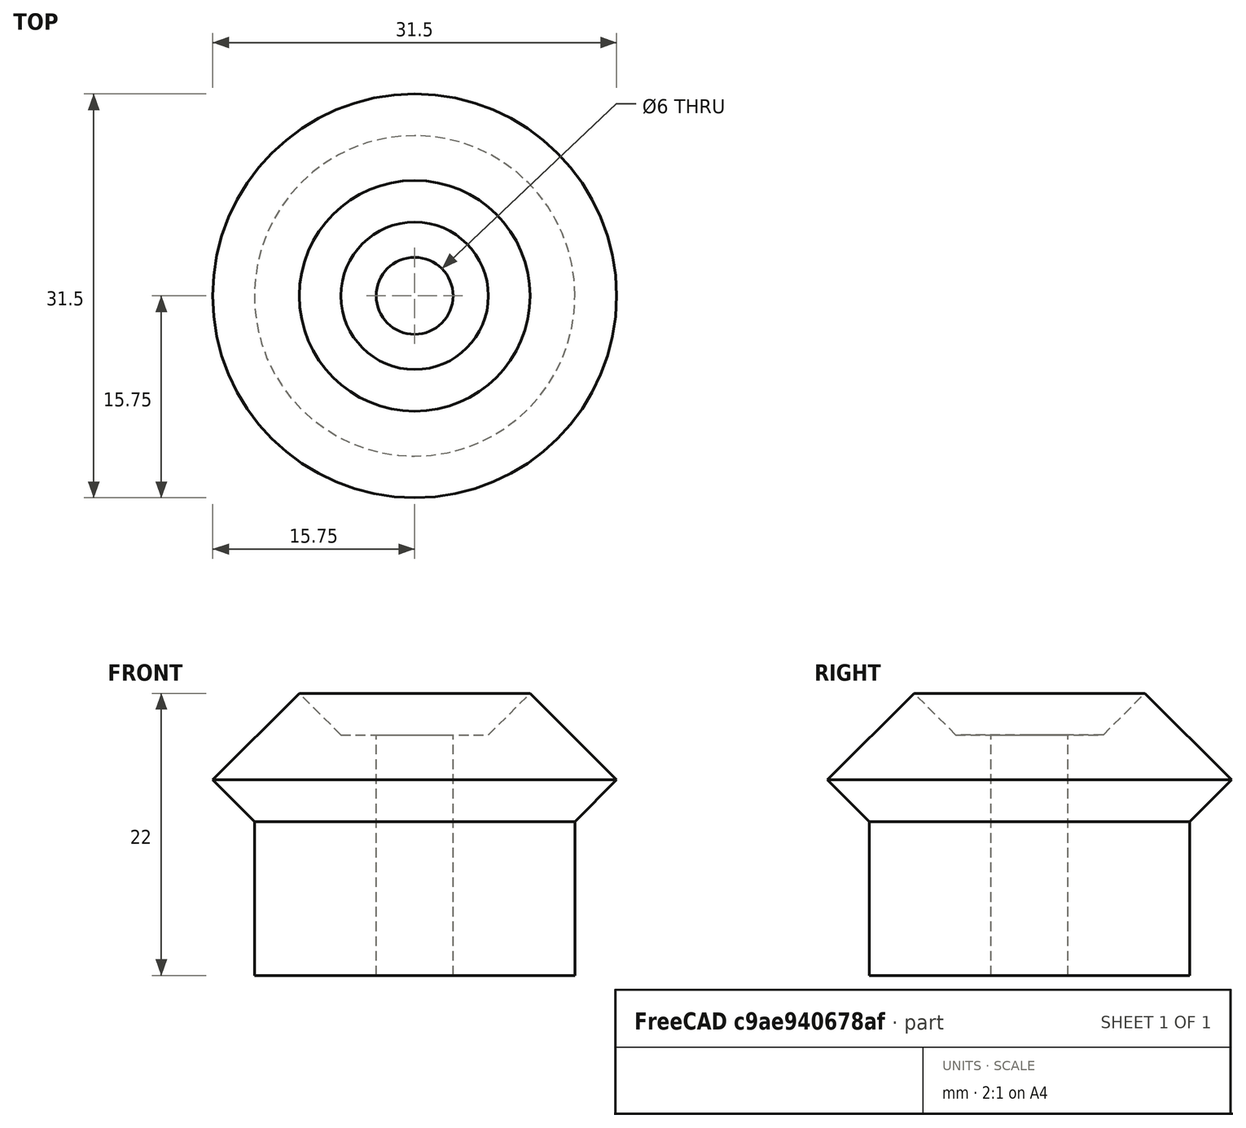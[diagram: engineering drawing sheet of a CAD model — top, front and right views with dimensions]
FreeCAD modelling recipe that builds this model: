
FCSTD DOCUMENT  (FreeCAD 0.18.4R)
Label: gear
License: All rights reserved
LicenseURL: http://en.wikipedia.org/wiki/All_rights_reserved
objects: Sketcher::SketchObject×1, PartDesign::Revolution×1, PartDesign::Body×1
note: 4 computed .brp shape members not serialized (recipe doc carries the construction recipe); baked Part::Feature solids carry a one-line shape summary decoded from their .brp

FEATURE [Sketcher::SketchObject] Sketch
  MapMode = 5
  Placement = pos=(0,0,0) rot=(1,0,0;1.5708rad)
  Support = -> [XZ_Plane]
  sketch-geometry (7):
    g0: LineSegment StartX=-3 StartY=18.75 StartZ=0 EndX=-5.75 EndY=18.75 EndZ=0
    g1: LineSegment StartX=-5.75 StartY=18.75 StartZ=0 EndX=-9 EndY=22 EndZ=0
    g2: LineSegment StartX=-9 StartY=22 StartZ=0 EndX=-15.75 EndY=15.25 EndZ=0
    g3: LineSegment StartX=-15.75 StartY=15.25 StartZ=0 EndX=-12.5 EndY=12 EndZ=0
    g4: LineSegment StartX=-12.5 StartY=12 StartZ=0 EndX=-12.5 EndY=0 EndZ=0
    g5: LineSegment StartX=-12.5 StartY=0 StartZ=0 EndX=-3 EndY=0 EndZ=0
    g6: LineSegment StartX=-3 StartY=0 StartZ=0 EndX=-3 EndY=18.75 EndZ=0
  constraints (21):
    c: Coincident(g0,g1)
    c: Coincident(g1,g2)
    c: Coincident(g2,g3)
    c: Coincident(g3,g4)
    c: Coincident(g4,g5)
    c: Coincident(g5,g6)
    c: Coincident(g6,g0)
    c: Vertical(g6)
    c: Horizontal(g5)
    c: Vertical(g4)
    c: Horizontal(g0)
    c: DistanceX(g0,g-1) = 3
    c: DistanceX(g4,g-1) = 12.5
    c: DistanceX(g2,g-1) = 15.75
    c: DistanceY(g4,g4) = 12
    c: DistanceY(g5,g1) = 22
    c: Angle(g2,g6) = 0.785398
    c: Perpendicular(g2,g1)
    c: Perpendicular(g2,g3)
    c: PointOnObject(g5,g-1)
    c: DistanceX(g0,g0) = 2.75
FEATURE [PartDesign::Revolution] Revolution
  Angle = 360
  Axis = (0,2e-16,1)
  Base = (0,0,0)
  Placement = pos=(0,0,0) rot=(1,0,0;1.5708rad)
  Profile = -> Sketch
  ReferenceAxis = -> Sketch [V_Axis]
FEATURE [PartDesign::Body] Body
  Group = -> [Sketch,Revolution]
  Origin = -> Origin
  Tip = -> Revolution
